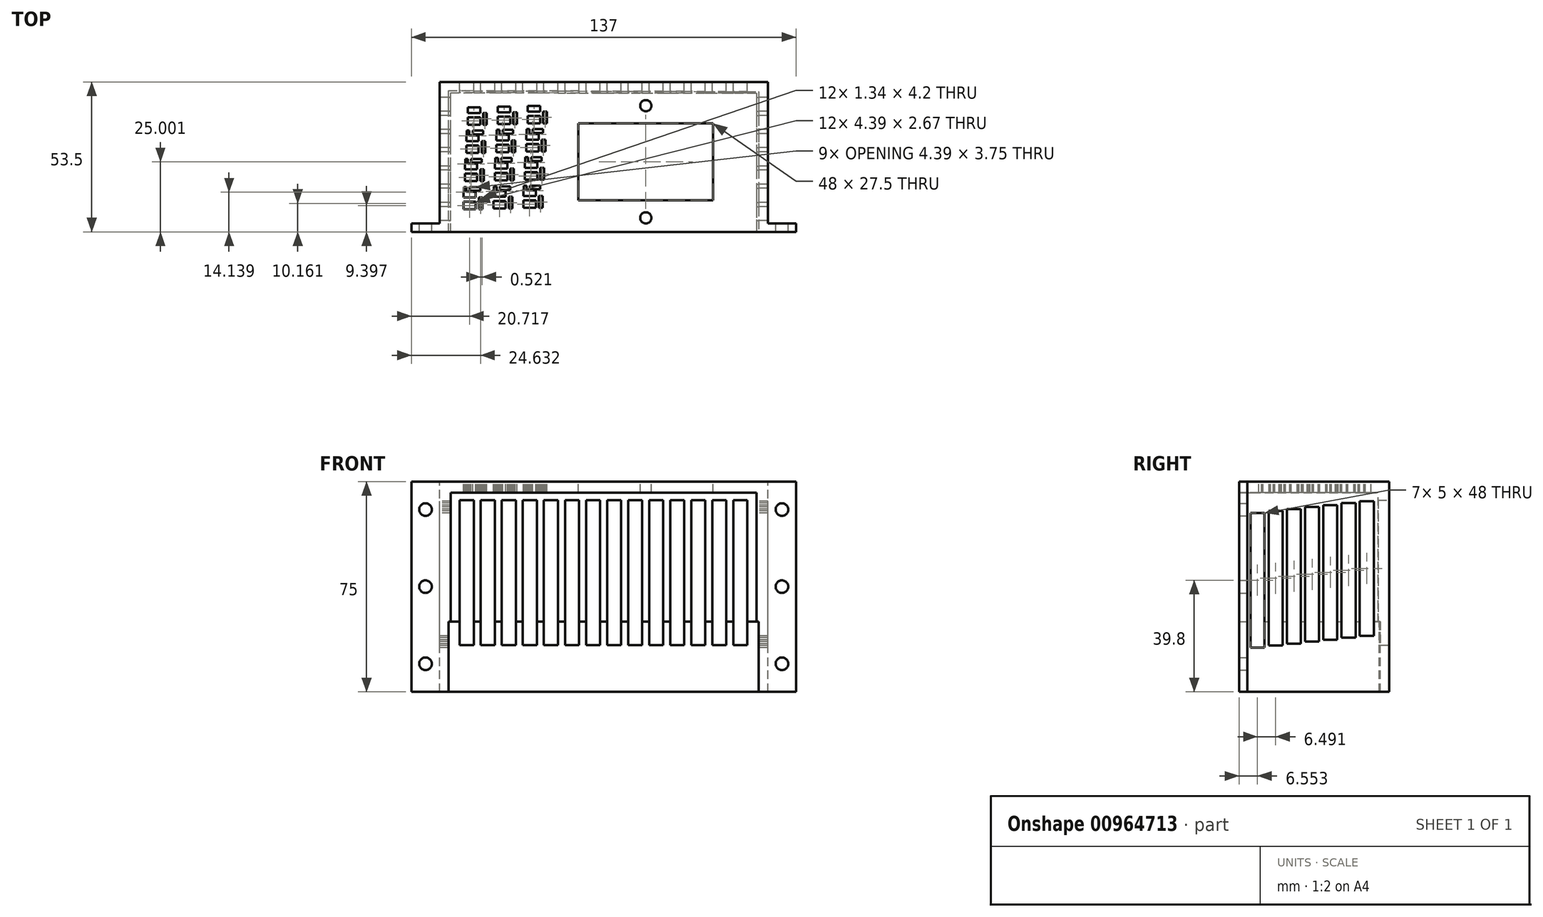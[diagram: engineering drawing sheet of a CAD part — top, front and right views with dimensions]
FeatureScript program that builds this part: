
annotation { "Feature Type Name" : "Feature", "Feature Type Description" : "" }
export const myFeature = defineFeature(function(context is Context, id is Id, definition is map)
    precondition{}
    {
        {
            var Q0;
            Q0=qCreatedBy(makeId("Top.planeOp"),FACE);
            var sketch = newSketch(context, id + "F0", { "sketchPlane" : qUnion([Q0])});
            skLineSegment(sketch, "E0.bottom", {"start": v(-95.4, 38.7) * mm, "end": v(21.6, 38.7) * mm});
            skLineSegment(sketch, "E0.top", {"start": v(-95.4, -14.8) * mm, "end": v(21.6, -14.8) * mm});
            skLineSegment(sketch, "E0.left", {"start": v(-95.4, 38.7) * mm, "end": v(-95.4, -11.8) * mm});
            skLineSegment(sketch, "E0.right", {"start": v(21.6, 38.7) * mm, "end": v(21.6, -11.8) * mm});
            skLineSegment(sketch, "E1.bottom", {"start": v(2.12, 23.94) * mm, "end": v(2.12, -3.56) * mm});
            skLineSegment(sketch, "E1.top", {"start": v(-45.88, 23.94) * mm, "end": v(-45.88, -3.56) * mm});
            skLineSegment(sketch, "E1.left", {"start": v(2.12, 23.94) * mm, "end": v(-45.88, 23.94) * mm});
            skLineSegment(sketch, "E1.right", {"start": v(2.12, -3.56) * mm, "end": v(-45.88, -3.56) * mm});
            skCircle(sketch, "E2", {"center": v(-21.88, 30.2) * mm, "radius": 2 * mm});
            skCircle(sketch, "E3", {"center": v(-21.88, -9.8) * mm, "radius": 2 * mm});
            skLineSegment(sketch, "E4", {"start": v(-45.88, 10.2) * mm, "end": v(2.12, 10.2) * mm, "construction": true});
            skLineSegment(sketch, "E5", {"start": v(7.87, 24.5) * mm, "end": v(7.87, -4.1) * mm});
            skLineSegment(sketch, "E6", {"start": v(-21.88, 23.94) * mm, "end": v(-21.88, -3.56) * mm, "construction": true});
            skLineSegment(sketch, "E7", {"start": v(-51.63, 24.5) * mm, "end": v(-51.63, -4.1) * mm});
            skPoint(sketch, "E8", {"position": v(-21.88, 34.7) * mm});
            skPoint(sketch, "E9", {"position": v(-21.88, -14.3) * mm});
            skLineSegment(sketch, "E10", {"start": v(-21.88, 34.7) * mm, "end": v(7.87, 24.5) * mm});
            skLineSegment(sketch, "E11", {"start": v(7.87, -4.1) * mm, "end": v(-21.88, -14.3) * mm});
            skLineSegment(sketch, "E12", {"start": v(-21.88, -14.3) * mm, "end": v(-51.63, -4.1) * mm});
            skLineSegment(sketch, "E13", {"start": v(-51.63, 24.5) * mm, "end": v(-21.88, 34.7) * mm});
            skPoint(sketch, "E14", {"position": v(-36.9, -14.8) * mm});
            skLineSegment(sketch, "E15", {"start": v(-91.4, -14.8) * mm, "end": v(-91.4, 34.8) * mm});
            skLineSegment(sketch, "E16", {"start": v(17.6, 34.7) * mm, "end": v(17.6, -14.8) * mm});
            skLineSegment(sketch, "E17", {"start": v(-91.4, 34.8) * mm, "end": v(17.6, 34.7) * mm});
            skLineSegment(sketch, "E18.2.0.0", {"start": v(-86.88, -4.08) * mm, "end": v(-82.49, -4.08) * mm});
            skLineSegment(sketch, "E18.2.0.1", {"start": v(-81.44, -2.55) * mm, "end": v(-81.44, -6.75) * mm});
            skLineSegment(sketch, "E18.2.0.3", {"start": v(-86.88, -4.08) * mm, "end": v(-86.88, -6.75) * mm});
            skLineSegment(sketch, "E18.2.0.4", {"start": v(-80.1, -2.55) * mm, "end": v(-80.1, -6.75) * mm});
            skLineSegment(sketch, "E18.2.0.5", {"start": v(-86.88, -2.55) * mm, "end": v(-82.49, -2.55) * mm});
            skLineSegment(sketch, "E18.2.0.7", {"start": v(-82.49, -4.08) * mm, "end": v(-82.49, -6.75) * mm});
            skLineSegment(sketch, "E18.2.0.9", {"start": v(-86.88, -0.54) * mm, "end": v(-82.49, -0.54) * mm});
            skLineSegment(sketch, "E18.2.0.11", {"start": v(-86.88, -6.75) * mm, "end": v(-82.49, -6.75) * mm});
            skLineSegment(sketch, "E18.2.0.14", {"start": v(-81.44, -2.55) * mm, "end": v(-80.1, -2.55) * mm});
            skLineSegment(sketch, "E18.2.0.16", {"start": v(-86.88, -0.54) * mm, "end": v(-86.88, -2.55) * mm});
            skLineSegment(sketch, "E18.2.0.17", {"start": v(-82.49, -0.54) * mm, "end": v(-82.49, -2.55) * mm});
            skLineSegment(sketch, "E18.2.0.19", {"start": v(-81.44, -6.75) * mm, "end": v(-80.1, -6.75) * mm});
            skLineSegment(sketch, "E18.2.1.0", {"start": v(-76.18, -3.82) * mm, "end": v(-71.8, -3.82) * mm});
            skLineSegment(sketch, "E18.2.1.1", {"start": v(-70.74, -2.29) * mm, "end": v(-70.74, -6.49) * mm});
            skLineSegment(sketch, "E18.2.1.3", {"start": v(-76.18, -3.82) * mm, "end": v(-76.18, -6.49) * mm});
            skLineSegment(sketch, "E18.2.1.4", {"start": v(-69.4, -2.29) * mm, "end": v(-69.4, -6.49) * mm});
            skLineSegment(sketch, "E18.2.1.5", {"start": v(-76.18, -2.29) * mm, "end": v(-71.8, -2.29) * mm});
            skLineSegment(sketch, "E18.2.1.7", {"start": v(-71.8, -3.82) * mm, "end": v(-71.8, -6.49) * mm});
            skLineSegment(sketch, "E18.2.1.9", {"start": v(-76.18, -0.28) * mm, "end": v(-71.8, -0.28) * mm});
            skLineSegment(sketch, "E18.2.1.11", {"start": v(-76.18, -6.49) * mm, "end": v(-71.8, -6.49) * mm});
            skLineSegment(sketch, "E18.2.1.14", {"start": v(-70.74, -2.29) * mm, "end": v(-69.4, -2.29) * mm});
            skLineSegment(sketch, "E18.2.1.16", {"start": v(-76.18, -0.28) * mm, "end": v(-76.18, -2.29) * mm});
            skLineSegment(sketch, "E18.2.1.17", {"start": v(-71.8, -0.28) * mm, "end": v(-71.8, -2.29) * mm});
            skLineSegment(sketch, "E18.2.1.19", {"start": v(-70.74, -6.49) * mm, "end": v(-69.4, -6.49) * mm});
            skLineSegment(sketch, "E18.2.2.0", {"start": v(-65.49, -3.56) * mm, "end": v(-61.1, -3.56) * mm});
            skLineSegment(sketch, "E18.2.2.1", {"start": v(-60.04, -2.03) * mm, "end": v(-60.04, -6.23) * mm});
            skLineSegment(sketch, "E18.2.2.3", {"start": v(-65.49, -3.56) * mm, "end": v(-65.49, -6.23) * mm});
            skLineSegment(sketch, "E18.2.2.4", {"start": v(-58.7, -2.03) * mm, "end": v(-58.7, -6.23) * mm});
            skLineSegment(sketch, "E18.2.2.5", {"start": v(-65.49, -2.03) * mm, "end": v(-61.1, -2.03) * mm});
            skLineSegment(sketch, "E18.2.2.7", {"start": v(-61.1, -3.56) * mm, "end": v(-61.1, -6.23) * mm});
            skLineSegment(sketch, "E18.2.2.9", {"start": v(-65.49, -0.02) * mm, "end": v(-61.1, -0.02) * mm});
            skLineSegment(sketch, "E18.2.2.11", {"start": v(-65.49, -6.23) * mm, "end": v(-61.1, -6.23) * mm});
            skLineSegment(sketch, "E18.2.2.14", {"start": v(-60.04, -2.03) * mm, "end": v(-58.7, -2.03) * mm});
            skLineSegment(sketch, "E18.2.2.16", {"start": v(-65.49, -0.02) * mm, "end": v(-65.49, -2.03) * mm});
            skLineSegment(sketch, "E18.2.2.17", {"start": v(-61.1, -0.02) * mm, "end": v(-61.1, -2.03) * mm});
            skLineSegment(sketch, "E18.2.2.19", {"start": v(-60.04, -6.23) * mm, "end": v(-58.7, -6.23) * mm});
            skLineSegment(sketch, "E18.3.0.0", {"start": v(-86.36, 5.98) * mm, "end": v(-81.97, 5.98) * mm});
            skLineSegment(sketch, "E18.3.0.1", {"start": v(-80.92, 7.5) * mm, "end": v(-80.92, 3.3) * mm});
            skLineSegment(sketch, "E18.3.0.2", {"start": v(-84.64, -0.13) * mm, "end": v(-80.92, -0.13) * mm});
            skLineSegment(sketch, "E18.3.0.3", {"start": v(-86.36, 5.98) * mm, "end": v(-86.36, 3.3) * mm});
            skLineSegment(sketch, "E18.3.0.4", {"start": v(-79.58, 7.5) * mm, "end": v(-79.58, 3.3) * mm});
            skLineSegment(sketch, "E18.3.0.5", {"start": v(-86.36, 7.5) * mm, "end": v(-81.97, 7.5) * mm});
            skLineSegment(sketch, "E18.3.0.6", {"start": v(-85.78, 1.2) * mm, "end": v(-85.78, -2.04) * mm});
            skLineSegment(sketch, "E18.3.0.7", {"start": v(-81.97, 5.98) * mm, "end": v(-81.97, 3.3) * mm});
            skLineSegment(sketch, "E18.3.0.8", {"start": v(-84.64, 1.2) * mm, "end": v(-80.92, 1.2) * mm});
            skLineSegment(sketch, "E18.3.0.9", {"start": v(-86.36, 9.51) * mm, "end": v(-81.97, 9.51) * mm});
            skLineSegment(sketch, "E18.3.0.10", {"start": v(-86.74, 1.2) * mm, "end": v(-86.74, -2.04) * mm});
            skLineSegment(sketch, "E18.3.0.11", {"start": v(-86.36, 3.3) * mm, "end": v(-81.97, 3.3) * mm});
            skLineSegment(sketch, "E18.3.0.12", {"start": v(-86.74, 1.2) * mm, "end": v(-85.78, 1.2) * mm});
            skLineSegment(sketch, "E18.3.0.13", {"start": v(-80.92, 1.2) * mm, "end": v(-80.92, -0.13) * mm});
            skLineSegment(sketch, "E18.3.0.14", {"start": v(-80.92, 7.5) * mm, "end": v(-79.58, 7.5) * mm});
            skLineSegment(sketch, "E18.3.0.15", {"start": v(-84.64, 1.2) * mm, "end": v(-84.64, -0.13) * mm});
            skLineSegment(sketch, "E18.3.0.16", {"start": v(-86.36, 9.51) * mm, "end": v(-86.36, 7.5) * mm});
            skLineSegment(sketch, "E18.3.0.17", {"start": v(-81.97, 9.51) * mm, "end": v(-81.97, 7.5) * mm});
            skLineSegment(sketch, "E18.3.0.18", {"start": v(-86.74, -2.04) * mm, "end": v(-85.78, -2.04) * mm});
            skLineSegment(sketch, "E18.3.0.19", {"start": v(-80.92, 3.3) * mm, "end": v(-79.58, 3.3) * mm});
            skLineSegment(sketch, "E18.3.1.0", {"start": v(-75.66, 6.24) * mm, "end": v(-71.27, 6.24) * mm});
            skLineSegment(sketch, "E18.3.1.1", {"start": v(-70.22, 7.77) * mm, "end": v(-70.22, 3.57) * mm});
            skLineSegment(sketch, "E18.3.1.2", {"start": v(-73.94, 0.13) * mm, "end": v(-70.22, 0.13) * mm});
            skLineSegment(sketch, "E18.3.1.3", {"start": v(-75.66, 6.24) * mm, "end": v(-75.66, 3.57) * mm});
            skLineSegment(sketch, "E18.3.1.4", {"start": v(-68.88, 7.77) * mm, "end": v(-68.88, 3.57) * mm});
            skLineSegment(sketch, "E18.3.1.5", {"start": v(-75.66, 7.77) * mm, "end": v(-71.27, 7.77) * mm});
            skLineSegment(sketch, "E18.3.1.6", {"start": v(-75.09, 1.47) * mm, "end": v(-75.09, -1.78) * mm});
            skLineSegment(sketch, "E18.3.1.7", {"start": v(-71.27, 6.24) * mm, "end": v(-71.27, 3.57) * mm});
            skLineSegment(sketch, "E18.3.1.8", {"start": v(-73.94, 1.47) * mm, "end": v(-70.22, 1.47) * mm});
            skLineSegment(sketch, "E18.3.1.9", {"start": v(-75.66, 9.77) * mm, "end": v(-71.27, 9.77) * mm});
            skLineSegment(sketch, "E18.3.1.10", {"start": v(-76.04, 1.47) * mm, "end": v(-76.04, -1.78) * mm});
            skLineSegment(sketch, "E18.3.1.11", {"start": v(-75.66, 3.57) * mm, "end": v(-71.27, 3.57) * mm});
            skLineSegment(sketch, "E18.3.1.12", {"start": v(-76.04, 1.47) * mm, "end": v(-75.09, 1.47) * mm});
            skLineSegment(sketch, "E18.3.1.13", {"start": v(-70.22, 1.47) * mm, "end": v(-70.22, 0.13) * mm});
            skLineSegment(sketch, "E18.3.1.14", {"start": v(-70.22, 7.77) * mm, "end": v(-68.88, 7.77) * mm});
            skLineSegment(sketch, "E18.3.1.15", {"start": v(-73.94, 1.47) * mm, "end": v(-73.94, 0.13) * mm});
            skLineSegment(sketch, "E18.3.1.16", {"start": v(-75.66, 9.77) * mm, "end": v(-75.66, 7.77) * mm});
            skLineSegment(sketch, "E18.3.1.17", {"start": v(-71.27, 9.77) * mm, "end": v(-71.27, 7.77) * mm});
            skLineSegment(sketch, "E18.3.1.18", {"start": v(-76.04, -1.78) * mm, "end": v(-75.09, -1.78) * mm});
            skLineSegment(sketch, "E18.3.1.19", {"start": v(-70.22, 3.57) * mm, "end": v(-68.88, 3.57) * mm});
            skLineSegment(sketch, "E18.3.2.0", {"start": v(-64.96, 6.5) * mm, "end": v(-60.57, 6.5) * mm});
            skLineSegment(sketch, "E18.3.2.1", {"start": v(-59.52, 8.03) * mm, "end": v(-59.52, 3.83) * mm});
            skLineSegment(sketch, "E18.3.2.2", {"start": v(-63.25, 0.39) * mm, "end": v(-59.52, 0.39) * mm});
            skLineSegment(sketch, "E18.3.2.3", {"start": v(-64.96, 6.5) * mm, "end": v(-64.96, 3.83) * mm});
            skLineSegment(sketch, "E18.3.2.4", {"start": v(-58.19, 8.03) * mm, "end": v(-58.19, 3.83) * mm});
            skLineSegment(sketch, "E18.3.2.5", {"start": v(-64.96, 8.03) * mm, "end": v(-60.57, 8.03) * mm});
            skLineSegment(sketch, "E18.3.2.6", {"start": v(-64.4, 1.73) * mm, "end": v(-64.4, -1.52) * mm});
            skLineSegment(sketch, "E18.3.2.7", {"start": v(-60.57, 6.5) * mm, "end": v(-60.57, 3.83) * mm});
            skLineSegment(sketch, "E18.3.2.8", {"start": v(-63.25, 1.73) * mm, "end": v(-59.52, 1.73) * mm});
            skLineSegment(sketch, "E18.3.2.9", {"start": v(-64.96, 10.03) * mm, "end": v(-60.57, 10.03) * mm});
            skLineSegment(sketch, "E18.3.2.10", {"start": v(-65.35, 1.73) * mm, "end": v(-65.35, -1.52) * mm});
            skLineSegment(sketch, "E18.3.2.11", {"start": v(-64.96, 3.83) * mm, "end": v(-60.57, 3.83) * mm});
            skLineSegment(sketch, "E18.3.2.12", {"start": v(-65.35, 1.73) * mm, "end": v(-64.4, 1.73) * mm});
            skLineSegment(sketch, "E18.3.2.13", {"start": v(-59.52, 1.73) * mm, "end": v(-59.52, 0.39) * mm});
            skLineSegment(sketch, "E18.3.2.14", {"start": v(-59.52, 8.03) * mm, "end": v(-58.19, 8.03) * mm});
            skLineSegment(sketch, "E18.3.2.15", {"start": v(-63.25, 1.73) * mm, "end": v(-63.25, 0.39) * mm});
            skLineSegment(sketch, "E18.3.2.16", {"start": v(-64.96, 10.03) * mm, "end": v(-64.96, 8.03) * mm});
            skLineSegment(sketch, "E18.3.2.17", {"start": v(-60.57, 10.03) * mm, "end": v(-60.57, 8.03) * mm});
            skLineSegment(sketch, "E18.3.2.18", {"start": v(-65.35, -1.52) * mm, "end": v(-64.4, -1.52) * mm});
            skLineSegment(sketch, "E18.3.2.19", {"start": v(-59.52, 3.83) * mm, "end": v(-58.19, 3.83) * mm});
            skLineSegment(sketch, "E18.4.0.0", {"start": v(-85.84, 16.04) * mm, "end": v(-81.44, 16.04) * mm});
            skLineSegment(sketch, "E18.4.0.1", {"start": v(-80.4, 17.56) * mm, "end": v(-80.4, 13.36) * mm});
            skLineSegment(sketch, "E18.4.0.2", {"start": v(-84.12, 9.93) * mm, "end": v(-80.4, 9.93) * mm});
            skLineSegment(sketch, "E18.4.0.3", {"start": v(-85.84, 16.04) * mm, "end": v(-85.84, 13.36) * mm});
            skLineSegment(sketch, "E18.4.0.4", {"start": v(-79.06, 17.56) * mm, "end": v(-79.06, 13.36) * mm});
            skLineSegment(sketch, "E18.4.0.5", {"start": v(-85.84, 17.56) * mm, "end": v(-81.44, 17.56) * mm});
            skLineSegment(sketch, "E18.4.0.6", {"start": v(-85.26, 11.26) * mm, "end": v(-85.26, 8.02) * mm});
            skLineSegment(sketch, "E18.4.0.7", {"start": v(-81.44, 16.04) * mm, "end": v(-81.44, 13.36) * mm});
            skLineSegment(sketch, "E18.4.0.8", {"start": v(-84.12, 11.26) * mm, "end": v(-80.4, 11.26) * mm});
            skLineSegment(sketch, "E18.4.0.9", {"start": v(-85.84, 19.57) * mm, "end": v(-81.44, 19.57) * mm});
            skLineSegment(sketch, "E18.4.0.10", {"start": v(-86.22, 11.26) * mm, "end": v(-86.22, 8.02) * mm});
            skLineSegment(sketch, "E18.4.0.11", {"start": v(-85.84, 13.36) * mm, "end": v(-81.44, 13.36) * mm});
            skLineSegment(sketch, "E18.4.0.12", {"start": v(-86.22, 11.26) * mm, "end": v(-85.26, 11.26) * mm});
            skLineSegment(sketch, "E18.4.0.13", {"start": v(-80.4, 11.26) * mm, "end": v(-80.4, 9.93) * mm});
            skLineSegment(sketch, "E18.4.0.14", {"start": v(-80.4, 17.56) * mm, "end": v(-79.06, 17.56) * mm});
            skLineSegment(sketch, "E18.4.0.15", {"start": v(-84.12, 11.26) * mm, "end": v(-84.12, 9.93) * mm});
            skLineSegment(sketch, "E18.4.0.16", {"start": v(-85.84, 19.57) * mm, "end": v(-85.84, 17.56) * mm});
            skLineSegment(sketch, "E18.4.0.17", {"start": v(-81.44, 19.57) * mm, "end": v(-81.44, 17.56) * mm});
            skLineSegment(sketch, "E18.4.0.18", {"start": v(-86.22, 8.02) * mm, "end": v(-85.26, 8.02) * mm});
            skLineSegment(sketch, "E18.4.0.19", {"start": v(-80.4, 13.36) * mm, "end": v(-79.06, 13.36) * mm});
            skLineSegment(sketch, "E18.4.1.0", {"start": v(-75.14, 16.3) * mm, "end": v(-70.75, 16.3) * mm});
            skLineSegment(sketch, "E18.4.1.1", {"start": v(-69.7, 17.82) * mm, "end": v(-69.7, 13.62) * mm});
            skLineSegment(sketch, "E18.4.1.2", {"start": v(-73.42, 10.19) * mm, "end": v(-69.7, 10.19) * mm});
            skLineSegment(sketch, "E18.4.1.3", {"start": v(-75.14, 16.3) * mm, "end": v(-75.14, 13.62) * mm});
            skLineSegment(sketch, "E18.4.1.4", {"start": v(-68.36, 17.82) * mm, "end": v(-68.36, 13.62) * mm});
            skLineSegment(sketch, "E18.4.1.5", {"start": v(-75.14, 17.82) * mm, "end": v(-70.75, 17.82) * mm});
            skLineSegment(sketch, "E18.4.1.6", {"start": v(-74.57, 11.52) * mm, "end": v(-74.57, 8.28) * mm});
            skLineSegment(sketch, "E18.4.1.7", {"start": v(-70.75, 16.3) * mm, "end": v(-70.75, 13.62) * mm});
            skLineSegment(sketch, "E18.4.1.8", {"start": v(-73.42, 11.52) * mm, "end": v(-69.7, 11.52) * mm});
            skLineSegment(sketch, "E18.4.1.9", {"start": v(-75.14, 19.83) * mm, "end": v(-70.75, 19.83) * mm});
            skLineSegment(sketch, "E18.4.1.10", {"start": v(-75.52, 11.52) * mm, "end": v(-75.52, 8.28) * mm});
            skLineSegment(sketch, "E18.4.1.11", {"start": v(-75.14, 13.62) * mm, "end": v(-70.75, 13.62) * mm});
            skLineSegment(sketch, "E18.4.1.12", {"start": v(-75.52, 11.52) * mm, "end": v(-74.57, 11.52) * mm});
            skLineSegment(sketch, "E18.4.1.13", {"start": v(-69.7, 11.52) * mm, "end": v(-69.7, 10.19) * mm});
            skLineSegment(sketch, "E18.4.1.14", {"start": v(-69.7, 17.82) * mm, "end": v(-68.36, 17.82) * mm});
            skLineSegment(sketch, "E18.4.1.15", {"start": v(-73.42, 11.52) * mm, "end": v(-73.42, 10.19) * mm});
            skLineSegment(sketch, "E18.4.1.16", {"start": v(-75.14, 19.83) * mm, "end": v(-75.14, 17.82) * mm});
            skLineSegment(sketch, "E18.4.1.17", {"start": v(-70.75, 19.83) * mm, "end": v(-70.75, 17.82) * mm});
            skLineSegment(sketch, "E18.4.1.18", {"start": v(-75.52, 8.28) * mm, "end": v(-74.57, 8.28) * mm});
            skLineSegment(sketch, "E18.4.1.19", {"start": v(-69.7, 13.62) * mm, "end": v(-68.36, 13.62) * mm});
            skLineSegment(sketch, "E18.4.2.0", {"start": v(-64.44, 16.56) * mm, "end": v(-60.05, 16.56) * mm});
            skLineSegment(sketch, "E18.4.2.1", {"start": v(-59, 18.08) * mm, "end": v(-59, 13.88) * mm});
            skLineSegment(sketch, "E18.4.2.2", {"start": v(-62.72, 10.45) * mm, "end": v(-59, 10.45) * mm});
            skLineSegment(sketch, "E18.4.2.3", {"start": v(-64.44, 16.56) * mm, "end": v(-64.44, 13.88) * mm});
            skLineSegment(sketch, "E18.4.2.4", {"start": v(-57.66, 18.08) * mm, "end": v(-57.66, 13.88) * mm});
            skLineSegment(sketch, "E18.4.2.5", {"start": v(-64.44, 18.08) * mm, "end": v(-60.05, 18.08) * mm});
            skLineSegment(sketch, "E18.4.2.6", {"start": v(-63.87, 11.78) * mm, "end": v(-63.87, 8.54) * mm});
            skLineSegment(sketch, "E18.4.2.7", {"start": v(-60.05, 16.56) * mm, "end": v(-60.05, 13.88) * mm});
            skLineSegment(sketch, "E18.4.2.8", {"start": v(-62.72, 11.78) * mm, "end": v(-59, 11.78) * mm});
            skLineSegment(sketch, "E18.4.2.9", {"start": v(-64.44, 20.09) * mm, "end": v(-60.05, 20.09) * mm});
            skLineSegment(sketch, "E18.4.2.10", {"start": v(-64.82, 11.78) * mm, "end": v(-64.82, 8.54) * mm});
            skLineSegment(sketch, "E18.4.2.11", {"start": v(-64.44, 13.88) * mm, "end": v(-60.05, 13.88) * mm});
            skLineSegment(sketch, "E18.4.2.12", {"start": v(-64.82, 11.78) * mm, "end": v(-63.87, 11.78) * mm});
            skLineSegment(sketch, "E18.4.2.13", {"start": v(-59, 11.78) * mm, "end": v(-59, 10.45) * mm});
            skLineSegment(sketch, "E18.4.2.14", {"start": v(-59, 18.08) * mm, "end": v(-57.66, 18.08) * mm});
            skLineSegment(sketch, "E18.4.2.15", {"start": v(-62.72, 11.78) * mm, "end": v(-62.72, 10.45) * mm});
            skLineSegment(sketch, "E18.4.2.16", {"start": v(-64.44, 20.09) * mm, "end": v(-64.44, 18.08) * mm});
            skLineSegment(sketch, "E18.4.2.17", {"start": v(-60.05, 20.09) * mm, "end": v(-60.05, 18.08) * mm});
            skLineSegment(sketch, "E18.4.2.18", {"start": v(-64.82, 8.54) * mm, "end": v(-63.87, 8.54) * mm});
            skLineSegment(sketch, "E18.4.2.19", {"start": v(-59, 13.88) * mm, "end": v(-57.66, 13.88) * mm});
            skLineSegment(sketch, "E18.5.0.0", {"start": v(-85.32, 26.1) * mm, "end": v(-80.92, 26.1) * mm});
            skLineSegment(sketch, "E18.5.0.1", {"start": v(-79.87, 27.62) * mm, "end": v(-79.87, 23.42) * mm});
            skLineSegment(sketch, "E18.5.0.2", {"start": v(-83.6, 19.98) * mm, "end": v(-79.87, 19.98) * mm});
            skLineSegment(sketch, "E18.5.0.3", {"start": v(-85.32, 26.1) * mm, "end": v(-85.32, 23.42) * mm});
            skLineSegment(sketch, "E18.5.0.4", {"start": v(-78.54, 27.62) * mm, "end": v(-78.54, 23.42) * mm});
            skLineSegment(sketch, "E18.5.0.5", {"start": v(-85.32, 27.62) * mm, "end": v(-80.92, 27.62) * mm});
            skLineSegment(sketch, "E18.5.0.6", {"start": v(-84.74, 21.32) * mm, "end": v(-84.74, 18.07) * mm});
            skLineSegment(sketch, "E18.5.0.7", {"start": v(-80.92, 26.1) * mm, "end": v(-80.92, 23.42) * mm});
            skLineSegment(sketch, "E18.5.0.8", {"start": v(-83.6, 21.32) * mm, "end": v(-79.87, 21.32) * mm});
            skLineSegment(sketch, "E18.5.0.9", {"start": v(-85.32, 29.62) * mm, "end": v(-80.92, 29.62) * mm});
            skLineSegment(sketch, "E18.5.0.10", {"start": v(-85.7, 21.32) * mm, "end": v(-85.7, 18.07) * mm});
            skLineSegment(sketch, "E18.5.0.11", {"start": v(-85.32, 23.42) * mm, "end": v(-80.92, 23.42) * mm});
            skLineSegment(sketch, "E18.5.0.12", {"start": v(-85.7, 21.32) * mm, "end": v(-84.74, 21.32) * mm});
            skLineSegment(sketch, "E18.5.0.13", {"start": v(-79.87, 21.32) * mm, "end": v(-79.87, 19.98) * mm});
            skLineSegment(sketch, "E18.5.0.14", {"start": v(-79.87, 27.62) * mm, "end": v(-78.54, 27.62) * mm});
            skLineSegment(sketch, "E18.5.0.15", {"start": v(-83.6, 21.32) * mm, "end": v(-83.6, 19.98) * mm});
            skLineSegment(sketch, "E18.5.0.16", {"start": v(-85.32, 29.62) * mm, "end": v(-85.32, 27.62) * mm});
            skLineSegment(sketch, "E18.5.0.17", {"start": v(-80.92, 29.62) * mm, "end": v(-80.92, 27.62) * mm});
            skLineSegment(sketch, "E18.5.0.18", {"start": v(-85.7, 18.07) * mm, "end": v(-84.74, 18.07) * mm});
            skLineSegment(sketch, "E18.5.0.19", {"start": v(-79.87, 23.42) * mm, "end": v(-78.54, 23.42) * mm});
            skLineSegment(sketch, "E18.5.1.0", {"start": v(-74.62, 26.35) * mm, "end": v(-70.23, 26.35) * mm});
            skLineSegment(sketch, "E18.5.1.1", {"start": v(-69.18, 27.88) * mm, "end": v(-69.18, 23.68) * mm});
            skLineSegment(sketch, "E18.5.1.2", {"start": v(-72.9, 20.24) * mm, "end": v(-69.18, 20.24) * mm});
            skLineSegment(sketch, "E18.5.1.3", {"start": v(-74.62, 26.35) * mm, "end": v(-74.62, 23.68) * mm});
            skLineSegment(sketch, "E18.5.1.4", {"start": v(-67.84, 27.88) * mm, "end": v(-67.84, 23.68) * mm});
            skLineSegment(sketch, "E18.5.1.5", {"start": v(-74.62, 27.88) * mm, "end": v(-70.23, 27.88) * mm});
            skLineSegment(sketch, "E18.5.1.6", {"start": v(-74.05, 21.58) * mm, "end": v(-74.05, 18.33) * mm});
            skLineSegment(sketch, "E18.5.1.7", {"start": v(-70.23, 26.35) * mm, "end": v(-70.23, 23.68) * mm});
            skLineSegment(sketch, "E18.5.1.8", {"start": v(-72.9, 21.58) * mm, "end": v(-69.18, 21.58) * mm});
            skLineSegment(sketch, "E18.5.1.9", {"start": v(-74.62, 29.89) * mm, "end": v(-70.23, 29.89) * mm});
            skLineSegment(sketch, "E18.5.1.10", {"start": v(-75, 21.58) * mm, "end": v(-75, 18.33) * mm});
            skLineSegment(sketch, "E18.5.1.11", {"start": v(-74.62, 23.68) * mm, "end": v(-70.23, 23.68) * mm});
            skLineSegment(sketch, "E18.5.1.12", {"start": v(-75, 21.58) * mm, "end": v(-74.05, 21.58) * mm});
            skLineSegment(sketch, "E18.5.1.13", {"start": v(-69.18, 21.58) * mm, "end": v(-69.18, 20.24) * mm});
            skLineSegment(sketch, "E18.5.1.14", {"start": v(-69.18, 27.88) * mm, "end": v(-67.84, 27.88) * mm});
            skLineSegment(sketch, "E18.5.1.15", {"start": v(-72.9, 21.58) * mm, "end": v(-72.9, 20.24) * mm});
            skLineSegment(sketch, "E18.5.1.16", {"start": v(-74.62, 29.89) * mm, "end": v(-74.62, 27.88) * mm});
            skLineSegment(sketch, "E18.5.1.17", {"start": v(-70.23, 29.89) * mm, "end": v(-70.23, 27.88) * mm});
            skLineSegment(sketch, "E18.5.1.18", {"start": v(-75, 18.33) * mm, "end": v(-74.05, 18.33) * mm});
            skLineSegment(sketch, "E18.5.1.19", {"start": v(-69.18, 23.68) * mm, "end": v(-67.84, 23.68) * mm});
            skLineSegment(sketch, "E18.5.2.0", {"start": v(-63.92, 26.61) * mm, "end": v(-59.53, 26.61) * mm});
            skLineSegment(sketch, "E18.5.2.1", {"start": v(-58.48, 28.14) * mm, "end": v(-58.48, 23.94) * mm});
            skLineSegment(sketch, "E18.5.2.2", {"start": v(-62.2, 20.5) * mm, "end": v(-58.48, 20.5) * mm});
            skLineSegment(sketch, "E18.5.2.3", {"start": v(-63.92, 26.61) * mm, "end": v(-63.92, 23.94) * mm});
            skLineSegment(sketch, "E18.5.2.4", {"start": v(-57.14, 28.14) * mm, "end": v(-57.14, 23.94) * mm});
            skLineSegment(sketch, "E18.5.2.5", {"start": v(-63.92, 28.14) * mm, "end": v(-59.53, 28.14) * mm});
            skLineSegment(sketch, "E18.5.2.6", {"start": v(-63.35, 21.84) * mm, "end": v(-63.35, 18.6) * mm});
            skLineSegment(sketch, "E18.5.2.7", {"start": v(-59.53, 26.61) * mm, "end": v(-59.53, 23.94) * mm});
            skLineSegment(sketch, "E18.5.2.8", {"start": v(-62.2, 21.84) * mm, "end": v(-58.48, 21.84) * mm});
            skLineSegment(sketch, "E18.5.2.9", {"start": v(-63.92, 30.15) * mm, "end": v(-59.53, 30.15) * mm});
            skLineSegment(sketch, "E18.5.2.10", {"start": v(-64.3, 21.84) * mm, "end": v(-64.3, 18.6) * mm});
            skLineSegment(sketch, "E18.5.2.11", {"start": v(-63.92, 23.94) * mm, "end": v(-59.53, 23.94) * mm});
            skLineSegment(sketch, "E18.5.2.12", {"start": v(-64.3, 21.84) * mm, "end": v(-63.35, 21.84) * mm});
            skLineSegment(sketch, "E18.5.2.13", {"start": v(-58.48, 21.84) * mm, "end": v(-58.48, 20.5) * mm});
            skLineSegment(sketch, "E18.5.2.14", {"start": v(-58.48, 28.14) * mm, "end": v(-57.14, 28.14) * mm});
            skLineSegment(sketch, "E18.5.2.15", {"start": v(-62.2, 21.84) * mm, "end": v(-62.2, 20.5) * mm});
            skLineSegment(sketch, "E18.5.2.16", {"start": v(-63.92, 30.15) * mm, "end": v(-63.92, 28.14) * mm});
            skLineSegment(sketch, "E18.5.2.17", {"start": v(-59.53, 30.15) * mm, "end": v(-59.53, 28.14) * mm});
            skLineSegment(sketch, "E18.5.2.18", {"start": v(-64.3, 18.6) * mm, "end": v(-63.35, 18.6) * mm});
            skLineSegment(sketch, "E18.5.2.19", {"start": v(-58.48, 23.94) * mm, "end": v(-57.14, 23.94) * mm});
            skLineSegment(sketch, "E19.bottom", {"start": v(-95.4, -14.8) * mm, "end": v(-105.4, -14.8) * mm});
            skLineSegment(sketch, "E19.top", {"start": v(-95.4, -11.8) * mm, "end": v(-105.4, -11.8) * mm});
            skLineSegment(sketch, "E19.right", {"start": v(-105.4, -14.8) * mm, "end": v(-105.4, -11.8) * mm});
            skLineSegment(sketch, "E20.bottom", {"start": v(21.6, -14.8) * mm, "end": v(31.6, -14.8) * mm});
            skLineSegment(sketch, "E20.top", {"start": v(21.6, -11.8) * mm, "end": v(31.6, -11.8) * mm});
            skLineSegment(sketch, "E20.right", {"start": v(31.6, -14.8) * mm, "end": v(31.6, -11.8) * mm});
            skSolve(sketch);
        }
        {
            var Q0;
            Q0=makeQuery(id+"F0.imprint","IMPRINT",FACE,{"disambiguationData":[TD([[makeQuery(id+"F0.imprint","IMPRINT",EDGE,{"derivedFrom":sQuery(id+"F0.wireOp",EDGE,"E0.bottom")}),-1.0]])]});
            extrude(context, id + "F1", {"entities" : qUnion([Q0]), "oppositeDirection" : true, "depth" : 50 * mm, "offsetDistance" : 25 * mm});
        }
        {
            var Q0;
            Q0=makeQuery(id+"F0.imprint","IMPRINT",FACE,{"disambiguationData":[TD([[makeQuery(id+"F0.imprint","IMPRINT",EDGE,{"derivedFrom":sQuery(id+"F0.wireOp",EDGE,"E5")}),1.0]])]});
            var Q1;
            Q1=makeQuery(id+"F0.imprint","IMPRINT",FACE,{"disambiguationData":[TD([[makeQuery(id+"F0.imprint","IMPRINT",EDGE,{"derivedFrom":sQuery(id+"F0.wireOp",EDGE,"E1.bottom")}),1.0]])]});
            extrude(context, id + "F2", {"entities" : qUnion([Q0, Q1]), "operationType" : NewBodyOperationType.ADD, "oppositeDirection" : true, "depth" : 4 * mm, "offsetDistance" : 25 * mm});
        }
        {
            var Q0;
            Q0=makeQuery(id+"F1.opExtrude","CAP_FACE",FACE,{"disambiguationData":[OSD([sQuery(id+"F0.wireOp",EDGE,"E0.bottom"),sQuery(id+"F0.wireOp",EDGE,"E0.top"),sQuery(id+"F0.wireOp",EDGE,"E0.left"),sQuery(id+"F0.wireOp",EDGE,"E0.right"),sQuery(id+"F0.wireOp",EDGE,"E15"),sQuery(id+"F0.wireOp",EDGE,"E16"),sQuery(id+"F0.wireOp",EDGE,"E17")])],"isStart":false});
            var sketch = newSketch(context, id + "F3", { "sketchPlane" : qUnion([Q0])});
            skLineSegment(sketch, "E21", {"start": v(-92.15, 14.8) * mm, "end": v(-92.15, -35.54) * mm});
            skLineSegment(sketch, "E22", {"start": v(-92.15, -35.54) * mm, "end": v(18.35, -35.2) * mm});
            skLineSegment(sketch, "E23", {"start": v(18.35, -35.2) * mm, "end": v(18.35, 14.8) * mm});
            skSolve(sketch);
        }
        {
            var Q0;
            {var subQ1=sQuery(id+"F3.wireOp",EDGE,"E21");Q0=makeQuery(id+"F3.imprint","IMPRINT",FACE,{"disambiguationData":[TD([[makeQuery(id+"F3.imprint","IMPRINT",EDGE,{"derivedFrom":subQ1}),-1.0]])]});}
            extrude(context, id + "F4", {"entities" : qUnion([Q0]), "operationType" : NewBodyOperationType.ADD, "depth" : 25 * mm, "offsetDistance" : 25 * mm});
        }
        {
            var Q0;
            {var subQ0=sQuery(id+"F0.wireOp",EDGE,"E20.top");Q0=makeQuery(id+"F4.boolean.opBoolean","MERGE",FACE,{"derivedFrom":[makeQuery(id+"F1.opExtrude","SWEPT_FACE",FACE,{"disambiguationData":[OSD([subQ0])]}),makeQuery(id+"F4.opExtrude","SWEPT_FACE",FACE,{"disambiguationData":[OSD([subQ0])]})]});}
            var sketch = newSketch(context, id + "F5", { "sketchPlane" : qUnion([Q0])});
            skLineSegment(sketch, "E24", {"start": v(-26.6, 0) * mm, "end": v(-26.6, -75) * mm, "construction": true});
            skLineSegment(sketch, "E25.0", {"start": v(95.4, 0) * mm, "end": v(105.4, 0) * mm});
            skLineSegment(sketch, "E25.1", {"start": v(95.4, -75) * mm, "end": v(105.4, -75) * mm});
            skLineSegment(sketch, "E26", {"start": v(100.4, 0) * mm, "end": v(100.4, -75) * mm, "construction": true});
            skLineSegment(sketch, "E27", {"start": v(100.4, -10) * mm, "end": v(-26.6, -10) * mm, "construction": true});
            skLineSegment(sketch, "E28", {"start": v(-26.6, -37.5) * mm, "end": v(100.4, -37.5) * mm, "construction": true});
            skPoint(sketch, "E28.endSnap0", {"position": v(100.4, -37.5) * mm});
            skLineSegment(sketch, "E29", {"start": v(100.4, -65) * mm, "end": v(-26.6, -65) * mm, "construction": true});
            skCircle(sketch, "E30", {"center": v(-26.6, -10) * mm, "radius": 2.25 * mm});
            skCircle(sketch, "E31", {"center": v(-26.6, -37.5) * mm, "radius": 2.25 * mm});
            skCircle(sketch, "E32", {"center": v(-26.6, -65) * mm, "radius": 2.25 * mm});
            skCircle(sketch, "E33", {"center": v(100.4, -10) * mm, "radius": 2.25 * mm});
            skCircle(sketch, "E34", {"center": v(100.4, -37.5) * mm, "radius": 2.25 * mm});
            skCircle(sketch, "E35", {"center": v(100.4, -65) * mm, "radius": 2.25 * mm});
            skSolve(sketch);
        }
        {
            var Q0;
            Q0=makeQuery(id+"F5.imprint","IMPRINT",FACE,{"disambiguationData":[TD([[makeQuery(id+"F5.imprint","IMPRINT",EDGE,{"derivedFrom":sQuery(id+"F5.wireOp",EDGE,"E30")}),1.0]])]});
            var Q1;
            Q1=makeQuery(id+"F5.imprint","IMPRINT",FACE,{"disambiguationData":[TD([[makeQuery(id+"F5.imprint","IMPRINT",EDGE,{"derivedFrom":sQuery(id+"F5.wireOp",EDGE,"E31")}),1.0]])]});
            var Q2;
            Q2=makeQuery(id+"F5.imprint","IMPRINT",FACE,{"disambiguationData":[TD([[makeQuery(id+"F5.imprint","IMPRINT",EDGE,{"derivedFrom":sQuery(id+"F5.wireOp",EDGE,"E32")}),1.0]])]});
            var Q3;
            Q3=makeQuery(id+"F5.imprint","IMPRINT",FACE,{"disambiguationData":[TD([[makeQuery(id+"F5.imprint","IMPRINT",EDGE,{"derivedFrom":sQuery(id+"F5.wireOp",EDGE,"E35")}),1.0]])]});
            var Q4;
            Q4=makeQuery(id+"F5.imprint","IMPRINT",FACE,{"disambiguationData":[TD([[makeQuery(id+"F5.imprint","IMPRINT",EDGE,{"derivedFrom":sQuery(id+"F5.wireOp",EDGE,"E34")}),1.0]])]});
            var Q5;
            Q5=makeQuery(id+"F5.imprint","IMPRINT",FACE,{"disambiguationData":[TD([[makeQuery(id+"F5.imprint","IMPRINT",EDGE,{"derivedFrom":sQuery(id+"F5.wireOp",EDGE,"E33")}),1.0]])]});
            extrude(context, id + "F6", {"entities" : qUnion([Q0, Q1, Q2, Q3, Q4, Q5]), "operationType" : NewBodyOperationType.REMOVE, "endBound" : BoundingType.THROUGH_ALL, "oppositeDirection" : true, "depth" : 25 * mm, "offsetDistance" : 25 * mm});
        }
        {
            var Q0;
            {var subQ0=sQuery(id+"F0.wireOp",EDGE,"E0.left");Q0=makeQuery(id+"F4.boolean.opBoolean","MERGE",FACE,{"derivedFrom":[makeQuery(id+"F1.opExtrude","SWEPT_FACE",FACE,{"disambiguationData":[OSD([subQ0])]}),makeQuery(id+"F4.opExtrude","SWEPT_FACE",FACE,{"disambiguationData":[OSD([subQ0])]})]});}
            var sketch = newSketch(context, id + "F7", { "sketchPlane" : qUnion([Q0])});
            skLineSegment(sketch, "E36", {"start": v(-38.7, -70) * mm, "end": v(11.8, -70) * mm, "construction": true});
            skLineSegment(sketch, "E37.0", {"start": v(14.8, -50) * mm, "end": v(-35.54, -50) * mm, "construction": true});
            skLineSegment(sketch, "E38.bottom", {"start": v(-33.2, -55) * mm, "end": v(-28.2, -55) * mm});
            skLineSegment(sketch, "E38.top", {"start": v(-33.2, -7) * mm, "end": v(-28.2, -7) * mm});
            skLineSegment(sketch, "E38.left", {"start": v(-33.2, -55) * mm, "end": v(-33.2, -7) * mm});
            skLineSegment(sketch, "E38.right", {"start": v(-28.2, -55) * mm, "end": v(-28.2, -7) * mm});
            skLineSegment(sketch, "E39.1.0.0", {"start": v(-21.7, -55.7) * mm, "end": v(-21.7, -7.7) * mm});
            skLineSegment(sketch, "E39.1.0.1", {"start": v(-26.7, -7.7) * mm, "end": v(-21.7, -7.7) * mm});
            skLineSegment(sketch, "E39.1.0.2", {"start": v(-26.7, -55.7) * mm, "end": v(-26.7, -7.7) * mm});
            skLineSegment(sketch, "E39.1.0.3", {"start": v(-26.7, -55.7) * mm, "end": v(-21.7, -55.7) * mm});
            skLineSegment(sketch, "E39.2.0.0", {"start": v(-15.2, -56.4) * mm, "end": v(-15.2, -8.4) * mm});
            skLineSegment(sketch, "E39.2.0.1", {"start": v(-20.2, -8.4) * mm, "end": v(-15.2, -8.4) * mm});
            skLineSegment(sketch, "E39.2.0.2", {"start": v(-20.2, -56.4) * mm, "end": v(-20.2, -8.4) * mm});
            skLineSegment(sketch, "E39.2.0.3", {"start": v(-20.2, -56.4) * mm, "end": v(-15.2, -56.4) * mm});
            skLineSegment(sketch, "E39.3.0.0", {"start": v(-8.72, -57.1) * mm, "end": v(-8.72, -9.1) * mm});
            skLineSegment(sketch, "E39.3.0.1", {"start": v(-13.72, -9.1) * mm, "end": v(-8.72, -9.1) * mm});
            skLineSegment(sketch, "E39.3.0.2", {"start": v(-13.72, -57.1) * mm, "end": v(-13.72, -9.1) * mm});
            skLineSegment(sketch, "E39.3.0.3", {"start": v(-13.72, -57.1) * mm, "end": v(-8.72, -57.1) * mm});
            skLineSegment(sketch, "E39.4.0.0", {"start": v(-2.23, -57.8) * mm, "end": v(-2.23, -9.8) * mm});
            skLineSegment(sketch, "E39.4.0.1", {"start": v(-7.23, -9.8) * mm, "end": v(-2.23, -9.8) * mm});
            skLineSegment(sketch, "E39.4.0.2", {"start": v(-7.23, -57.8) * mm, "end": v(-7.23, -9.8) * mm});
            skLineSegment(sketch, "E39.4.0.3", {"start": v(-7.23, -57.8) * mm, "end": v(-2.23, -57.8) * mm});
            skLineSegment(sketch, "E39.5.0.0", {"start": v(4.27, -58.5) * mm, "end": v(4.27, -10.5) * mm});
            skLineSegment(sketch, "E39.5.0.1", {"start": v(-0.73, -10.5) * mm, "end": v(4.27, -10.5) * mm});
            skLineSegment(sketch, "E39.5.0.2", {"start": v(-0.73, -58.5) * mm, "end": v(-0.73, -10.5) * mm});
            skLineSegment(sketch, "E39.5.0.3", {"start": v(-0.73, -58.5) * mm, "end": v(4.27, -58.5) * mm});
            skLineSegment(sketch, "E39.6.0.0", {"start": v(10.76, -59.2) * mm, "end": v(10.76, -11.2) * mm});
            skLineSegment(sketch, "E39.6.0.1", {"start": v(5.76, -11.2) * mm, "end": v(10.76, -11.2) * mm});
            skLineSegment(sketch, "E39.6.0.2", {"start": v(5.76, -59.2) * mm, "end": v(5.76, -11.2) * mm});
            skLineSegment(sketch, "E39.6.0.3", {"start": v(5.76, -59.2) * mm, "end": v(10.76, -59.2) * mm});
            skLineSegment(sketch, "E39.direction1", {"start": v(-28.2, -55) * mm, "end": v(-21.7, -55.7) * mm, "construction": true});
            skSolve(sketch);
        }
        {
            var Q0;
            Q0=makeQuery(id+"F7.imprint","IMPRINT",FACE,{"disambiguationData":[TD([[makeQuery(id+"F7.imprint","IMPRINT",EDGE,{"derivedFrom":sQuery(id+"F7.wireOp",EDGE,"E38.bottom")}),1.0]])]});
            var Q1;
            Q1=makeQuery(id+"F7.imprint","IMPRINT",FACE,{"disambiguationData":[TD([[makeQuery(id+"F7.imprint","IMPRINT",EDGE,{"derivedFrom":sQuery(id+"F7.wireOp",EDGE,"E39.1.0.0")}),1.0]])]});
            var Q2;
            Q2=makeQuery(id+"F7.imprint","IMPRINT",FACE,{"disambiguationData":[TD([[makeQuery(id+"F7.imprint","IMPRINT",EDGE,{"derivedFrom":sQuery(id+"F7.wireOp",EDGE,"E39.2.0.0")}),1.0]])]});
            var Q3;
            Q3=makeQuery(id+"F7.imprint","IMPRINT",FACE,{"disambiguationData":[TD([[makeQuery(id+"F7.imprint","IMPRINT",EDGE,{"derivedFrom":sQuery(id+"F7.wireOp",EDGE,"E39.3.0.0")}),1.0]])]});
            var Q4;
            Q4=makeQuery(id+"F7.imprint","IMPRINT",FACE,{"disambiguationData":[TD([[makeQuery(id+"F7.imprint","IMPRINT",EDGE,{"derivedFrom":sQuery(id+"F7.wireOp",EDGE,"E39.4.0.0")}),1.0]])]});
            var Q5;
            Q5=makeQuery(id+"F7.imprint","IMPRINT",FACE,{"disambiguationData":[TD([[makeQuery(id+"F7.imprint","IMPRINT",EDGE,{"derivedFrom":sQuery(id+"F7.wireOp",EDGE,"E39.5.0.0")}),1.0]])]});
            var Q6;
            Q6=makeQuery(id+"F7.imprint","IMPRINT",FACE,{"disambiguationData":[TD([[makeQuery(id+"F7.imprint","IMPRINT",EDGE,{"derivedFrom":sQuery(id+"F7.wireOp",EDGE,"E39.6.0.0")}),1.0]])]});
            extrude(context, id + "F8", {"entities" : qUnion([Q0, Q1, Q2, Q3, Q4, Q5, Q6]), "operationType" : NewBodyOperationType.REMOVE, "endBound" : BoundingType.THROUGH_ALL, "oppositeDirection" : true, "depth" : 25 * mm, "offsetDistance" : 25 * mm});
        }
        {
            var Q0;
            {var subQ0=sQuery(id+"F0.wireOp",EDGE,"E0.bottom");Q0=makeQuery(id+"F4.boolean.opBoolean","MERGE",FACE,{"derivedFrom":[makeQuery(id+"F1.opExtrude","SWEPT_FACE",FACE,{"disambiguationData":[OSD([subQ0])]}),makeQuery(id+"F4.opExtrude","SWEPT_FACE",FACE,{"disambiguationData":[OSD([subQ0])]})]});}
            var sketch = newSketch(context, id + "F9", { "sketchPlane" : qUnion([Q0])});
            skLineSegment(sketch, "E40.bottom", {"start": v(88.2, -58.34) * mm, "end": v(83.2, -58.34) * mm});
            skLineSegment(sketch, "E40.top", {"start": v(88.2, -6.7) * mm, "end": v(83.2, -6.7) * mm});
            skLineSegment(sketch, "E40.left", {"start": v(88.2, -58.34) * mm, "end": v(88.2, -6.7) * mm});
            skLineSegment(sketch, "E40.right", {"start": v(83.2, -58.34) * mm, "end": v(83.2, -6.7) * mm});
            skLineSegment(sketch, "E41.1.0.0", {"start": v(80.7, -58.34) * mm, "end": v(80.7, -6.7) * mm});
            skLineSegment(sketch, "E41.1.0.1", {"start": v(75.7, -58.34) * mm, "end": v(75.7, -6.7) * mm});
            skLineSegment(sketch, "E41.1.0.2", {"start": v(80.7, -58.34) * mm, "end": v(75.7, -58.34) * mm});
            skLineSegment(sketch, "E41.1.0.3", {"start": v(80.7, -6.7) * mm, "end": v(75.7, -6.7) * mm});
            skLineSegment(sketch, "E41.2.0.0", {"start": v(73.2, -58.34) * mm, "end": v(73.2, -6.7) * mm});
            skLineSegment(sketch, "E41.2.0.1", {"start": v(68.2, -58.34) * mm, "end": v(68.2, -6.7) * mm});
            skLineSegment(sketch, "E41.2.0.2", {"start": v(73.2, -58.34) * mm, "end": v(68.2, -58.34) * mm});
            skLineSegment(sketch, "E41.2.0.3", {"start": v(73.2, -6.7) * mm, "end": v(68.2, -6.7) * mm});
            skLineSegment(sketch, "E41.3.0.0", {"start": v(65.7, -58.34) * mm, "end": v(65.7, -6.7) * mm});
            skLineSegment(sketch, "E41.3.0.1", {"start": v(60.7, -58.34) * mm, "end": v(60.7, -6.7) * mm});
            skLineSegment(sketch, "E41.3.0.2", {"start": v(65.7, -58.34) * mm, "end": v(60.7, -58.34) * mm});
            skLineSegment(sketch, "E41.3.0.3", {"start": v(65.7, -6.7) * mm, "end": v(60.7, -6.7) * mm});
            skLineSegment(sketch, "E41.4.0.0", {"start": v(58.2, -58.34) * mm, "end": v(58.2, -6.7) * mm});
            skLineSegment(sketch, "E41.4.0.1", {"start": v(53.2, -58.34) * mm, "end": v(53.2, -6.7) * mm});
            skLineSegment(sketch, "E41.4.0.2", {"start": v(58.2, -58.34) * mm, "end": v(53.2, -58.34) * mm});
            skLineSegment(sketch, "E41.4.0.3", {"start": v(58.2, -6.7) * mm, "end": v(53.2, -6.7) * mm});
            skLineSegment(sketch, "E41.5.0.0", {"start": v(50.7, -58.34) * mm, "end": v(50.7, -6.7) * mm});
            skLineSegment(sketch, "E41.5.0.1", {"start": v(45.7, -58.34) * mm, "end": v(45.7, -6.7) * mm});
            skLineSegment(sketch, "E41.5.0.2", {"start": v(50.7, -58.34) * mm, "end": v(45.7, -58.34) * mm});
            skLineSegment(sketch, "E41.5.0.3", {"start": v(50.7, -6.7) * mm, "end": v(45.7, -6.7) * mm});
            skLineSegment(sketch, "E41.6.0.0", {"start": v(43.2, -58.34) * mm, "end": v(43.2, -6.7) * mm});
            skLineSegment(sketch, "E41.6.0.1", {"start": v(38.2, -58.34) * mm, "end": v(38.2, -6.7) * mm});
            skLineSegment(sketch, "E41.6.0.2", {"start": v(43.2, -58.34) * mm, "end": v(38.2, -58.34) * mm});
            skLineSegment(sketch, "E41.6.0.3", {"start": v(43.2, -6.7) * mm, "end": v(38.2, -6.7) * mm});
            skLineSegment(sketch, "E41.7.0.0", {"start": v(35.7, -58.34) * mm, "end": v(35.7, -6.7) * mm});
            skLineSegment(sketch, "E41.7.0.1", {"start": v(30.7, -58.34) * mm, "end": v(30.7, -6.7) * mm});
            skLineSegment(sketch, "E41.7.0.2", {"start": v(35.7, -58.34) * mm, "end": v(30.7, -58.34) * mm});
            skLineSegment(sketch, "E41.7.0.3", {"start": v(35.7, -6.7) * mm, "end": v(30.7, -6.7) * mm});
            skLineSegment(sketch, "E41.8.0.0", {"start": v(28.2, -58.34) * mm, "end": v(28.2, -6.7) * mm});
            skLineSegment(sketch, "E41.8.0.1", {"start": v(23.2, -58.34) * mm, "end": v(23.2, -6.7) * mm});
            skLineSegment(sketch, "E41.8.0.2", {"start": v(28.2, -58.34) * mm, "end": v(23.2, -58.34) * mm});
            skLineSegment(sketch, "E41.8.0.3", {"start": v(28.2, -6.7) * mm, "end": v(23.2, -6.7) * mm});
            skLineSegment(sketch, "E41.9.0.0", {"start": v(20.7, -58.34) * mm, "end": v(20.7, -6.7) * mm});
            skLineSegment(sketch, "E41.9.0.1", {"start": v(15.7, -58.34) * mm, "end": v(15.7, -6.7) * mm});
            skLineSegment(sketch, "E41.9.0.2", {"start": v(20.7, -58.34) * mm, "end": v(15.7, -58.34) * mm});
            skLineSegment(sketch, "E41.9.0.3", {"start": v(20.7, -6.7) * mm, "end": v(15.7, -6.7) * mm});
            skLineSegment(sketch, "E41.10.0.0", {"start": v(13.2, -58.34) * mm, "end": v(13.2, -6.7) * mm});
            skLineSegment(sketch, "E41.10.0.1", {"start": v(8.2, -58.34) * mm, "end": v(8.2, -6.7) * mm});
            skLineSegment(sketch, "E41.10.0.2", {"start": v(13.2, -58.34) * mm, "end": v(8.2, -58.34) * mm});
            skLineSegment(sketch, "E41.10.0.3", {"start": v(13.2, -6.7) * mm, "end": v(8.2, -6.7) * mm});
            skLineSegment(sketch, "E41.11.0.0", {"start": v(5.7, -58.34) * mm, "end": v(5.7, -6.7) * mm});
            skLineSegment(sketch, "E41.11.0.1", {"start": v(0.7, -58.34) * mm, "end": v(0.7, -6.7) * mm});
            skLineSegment(sketch, "E41.11.0.2", {"start": v(5.7, -58.34) * mm, "end": v(0.7, -58.34) * mm});
            skLineSegment(sketch, "E41.11.0.3", {"start": v(5.7, -6.7) * mm, "end": v(0.7, -6.7) * mm});
            skLineSegment(sketch, "E41.12.0.0", {"start": v(-1.8, -58.34) * mm, "end": v(-1.8, -6.7) * mm});
            skLineSegment(sketch, "E41.12.0.1", {"start": v(-6.8, -58.34) * mm, "end": v(-6.8, -6.7) * mm});
            skLineSegment(sketch, "E41.12.0.2", {"start": v(-1.8, -58.34) * mm, "end": v(-6.8, -58.34) * mm});
            skLineSegment(sketch, "E41.12.0.3", {"start": v(-1.8, -6.7) * mm, "end": v(-6.8, -6.7) * mm});
            skLineSegment(sketch, "E41.13.0.0", {"start": v(-9.3, -58.34) * mm, "end": v(-9.3, -6.7) * mm});
            skLineSegment(sketch, "E41.13.0.1", {"start": v(-14.3, -58.34) * mm, "end": v(-14.3, -6.7) * mm});
            skLineSegment(sketch, "E41.13.0.2", {"start": v(-9.3, -58.34) * mm, "end": v(-14.3, -58.34) * mm});
            skLineSegment(sketch, "E41.13.0.3", {"start": v(-9.3, -6.7) * mm, "end": v(-14.3, -6.7) * mm});
            skLineSegment(sketch, "E41.direction1", {"start": v(88.2, -58.34) * mm, "end": v(80.7, -58.34) * mm, "construction": true});
            skSolve(sketch);
        }
        {
            var Q0;
            Q0=makeQuery(id+"F9.imprint","IMPRINT",FACE,{"disambiguationData":[TD([[makeQuery(id+"F9.imprint","IMPRINT",EDGE,{"derivedFrom":sQuery(id+"F9.wireOp",EDGE,"E40.bottom")}),-1.0]])]});
            var Q1;
            Q1=makeQuery(id+"F9.imprint","IMPRINT",FACE,{"disambiguationData":[TD([[makeQuery(id+"F9.imprint","IMPRINT",EDGE,{"derivedFrom":sQuery(id+"F9.wireOp",EDGE,"E41.1.0.0")}),1.0]])]});
            var Q2;
            Q2=makeQuery(id+"F9.imprint","IMPRINT",FACE,{"disambiguationData":[TD([[makeQuery(id+"F9.imprint","IMPRINT",EDGE,{"derivedFrom":sQuery(id+"F9.wireOp",EDGE,"E41.2.0.0")}),1.0]])]});
            var Q3;
            Q3=makeQuery(id+"F9.imprint","IMPRINT",FACE,{"disambiguationData":[TD([[makeQuery(id+"F9.imprint","IMPRINT",EDGE,{"derivedFrom":sQuery(id+"F9.wireOp",EDGE,"E41.3.0.0")}),1.0]])]});
            var Q4;
            Q4=makeQuery(id+"F9.imprint","IMPRINT",FACE,{"disambiguationData":[TD([[makeQuery(id+"F9.imprint","IMPRINT",EDGE,{"derivedFrom":sQuery(id+"F9.wireOp",EDGE,"E41.4.0.0")}),1.0]])]});
            var Q5;
            Q5=makeQuery(id+"F9.imprint","IMPRINT",FACE,{"disambiguationData":[TD([[makeQuery(id+"F9.imprint","IMPRINT",EDGE,{"derivedFrom":sQuery(id+"F9.wireOp",EDGE,"E41.5.0.0")}),1.0]])]});
            var Q6;
            Q6=makeQuery(id+"F9.imprint","IMPRINT",FACE,{"disambiguationData":[TD([[makeQuery(id+"F9.imprint","IMPRINT",EDGE,{"derivedFrom":sQuery(id+"F9.wireOp",EDGE,"E41.6.0.0")}),1.0]])]});
            var Q7;
            Q7=makeQuery(id+"F9.imprint","IMPRINT",FACE,{"disambiguationData":[TD([[makeQuery(id+"F9.imprint","IMPRINT",EDGE,{"derivedFrom":sQuery(id+"F9.wireOp",EDGE,"E41.7.0.0")}),1.0]])]});
            var Q8;
            Q8=makeQuery(id+"F9.imprint","IMPRINT",FACE,{"disambiguationData":[TD([[makeQuery(id+"F9.imprint","IMPRINT",EDGE,{"derivedFrom":sQuery(id+"F9.wireOp",EDGE,"E41.8.0.0")}),1.0]])]});
            var Q9;
            Q9=makeQuery(id+"F9.imprint","IMPRINT",FACE,{"disambiguationData":[TD([[makeQuery(id+"F9.imprint","IMPRINT",EDGE,{"derivedFrom":sQuery(id+"F9.wireOp",EDGE,"E41.9.0.0")}),1.0]])]});
            var Q10;
            Q10=makeQuery(id+"F9.imprint","IMPRINT",FACE,{"disambiguationData":[TD([[makeQuery(id+"F9.imprint","IMPRINT",EDGE,{"derivedFrom":sQuery(id+"F9.wireOp",EDGE,"E41.10.0.0")}),1.0]])]});
            var Q11;
            Q11=makeQuery(id+"F9.imprint","IMPRINT",FACE,{"disambiguationData":[TD([[makeQuery(id+"F9.imprint","IMPRINT",EDGE,{"derivedFrom":sQuery(id+"F9.wireOp",EDGE,"E41.11.0.0")}),1.0]])]});
            var Q12;
            Q12=makeQuery(id+"F9.imprint","IMPRINT",FACE,{"disambiguationData":[TD([[makeQuery(id+"F9.imprint","IMPRINT",EDGE,{"derivedFrom":sQuery(id+"F9.wireOp",EDGE,"E41.12.0.0")}),1.0]])]});
            var Q13;
            Q13=makeQuery(id+"F9.imprint","IMPRINT",FACE,{"disambiguationData":[TD([[makeQuery(id+"F9.imprint","IMPRINT",EDGE,{"derivedFrom":sQuery(id+"F9.wireOp",EDGE,"E41.13.0.0")}),1.0]])]});
            extrude(context, id + "F10", {"entities" : qUnion([Q0, Q1, Q2, Q3, Q4, Q5, Q6, Q7, Q8, Q9, Q10, Q11, Q12, Q13]), "operationType" : NewBodyOperationType.REMOVE, "endBound" : BoundingType.THROUGH_ALL, "oppositeDirection" : true, "depth" : 25 * mm, "offsetDistance" : 25 * mm});
        }
    });
